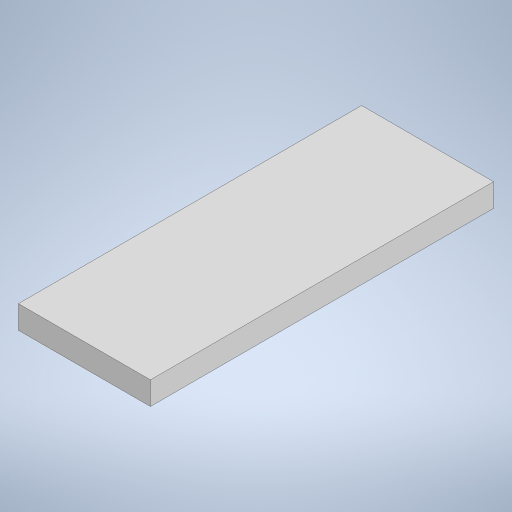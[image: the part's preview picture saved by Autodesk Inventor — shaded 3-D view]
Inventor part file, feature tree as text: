
AUTODESK INVENTOR PART (.ipt)
format: ipt  version: 2023 (Build 270158000, 158)  size: 201,728 bytes
history: native  units: mm
features: extrude x1, sketch x1
ambient origin geometry x8: Origin, YZ Plane, XZ Plane, XY Plane, X Axis, Y Axis, Z Axis, Center Point
bodies: Solid1 (feature_tree)
feature tree (2):
  extrude  "Extrusion1"  Depth=200.0mm
  sketch  "Sketch1"  dims[d0=520.0mm d1=200.0mm d2=35.0mm d3=0.0mm]
